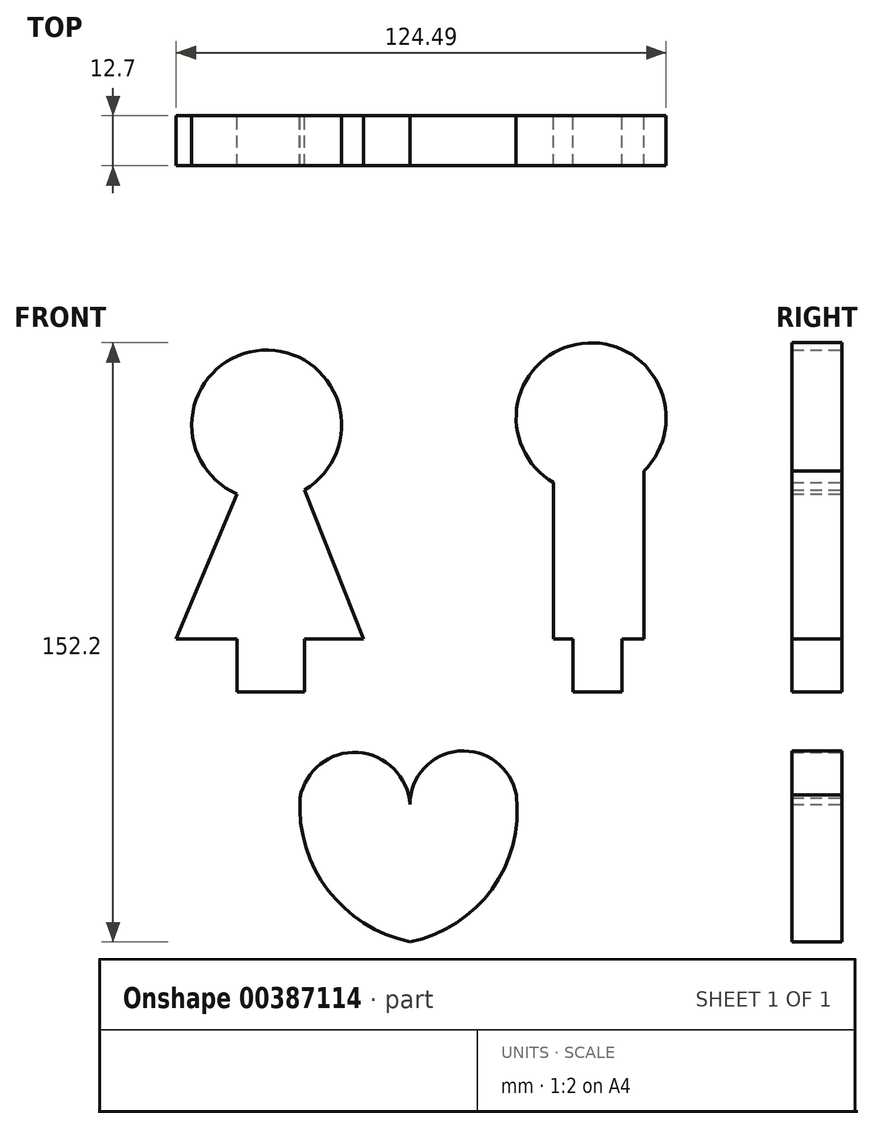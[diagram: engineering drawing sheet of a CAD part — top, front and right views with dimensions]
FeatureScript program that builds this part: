
annotation { "Feature Type Name" : "Feature", "Feature Type Description" : "" }
export const myFeature = defineFeature(function(context is Context, id is Id, definition is map)
    precondition{}
    {
        {
            var Q0;
            Q0=qCreatedBy(makeId("Front.planeOp"),FACE);
            var sketch = newSketch(context, id + "F0", { "sketchPlane" : qUnion([Q0])});
            skCircle(sketch, "E0", {"center": v(-36.38, 54.42) * mm, "radius": 19.05 * mm});
            skCircle(sketch, "E1", {"center": v(46.05, 56.26) * mm, "radius": 19.05 * mm});
            skLineSegment(sketch, "E2", {"start": v(-43.94, 36.93) * mm, "end": v(-59.39, 0) * mm});
            skLineSegment(sketch, "E3", {"start": v(-26.78, 37.97) * mm, "end": v(-11.72, 0) * mm});
            skLineSegment(sketch, "E4", {"start": v(36.5, 39.78) * mm, "end": v(36.5, 0) * mm});
            skLineSegment(sketch, "E5", {"start": v(59.4, 42.67) * mm, "end": v(59.4, 0) * mm});
            skLineSegment(sketch, "E6", {"start": v(-59.39, 0) * mm, "end": v(-11.72, 0) * mm});
            skLineSegment(sketch, "E7", {"start": v(36.5, 0) * mm, "end": v(59.4, 0) * mm});
            skLineSegment(sketch, "E8", {"start": v(-36.38, 0) * mm, "end": v(-36.38, -13.38) * mm});
            skLineSegment(sketch, "E9", {"start": v(-43.94, 0) * mm, "end": v(-43.94, -13.38) * mm});
            skLineSegment(sketch, "E10", {"start": v(-26.78, -13.38) * mm, "end": v(-43.94, -13.38) * mm});
            skLineSegment(sketch, "E11", {"start": v(-26.78, -13.38) * mm, "end": v(-26.78, 0) * mm});
            skLineSegment(sketch, "E12", {"start": v(41.44, -13.38) * mm, "end": v(41.44, 0) * mm});
            skLineSegment(sketch, "E13", {"start": v(53.9, 0) * mm, "end": v(53.9, -13.38) * mm});
            skLineSegment(sketch, "E14", {"start": v(41.44, -13.38) * mm, "end": v(53.9, -13.38) * mm});
            skLineSegment(sketch, "E15", {"start": v(47.68, -13.38) * mm, "end": v(47.68, 0) * mm});
            skPoint(sketch, "E16", {"position": v(0, -76.9) * mm});
            skArc(sketch, "E17", {"start": v(0, -42.01) * mm, "mid": v(-13.2, -28.8) * mm, "end": v(-27.92, -40.28) * mm});
            skArc(sketch, "E18", {"start": v(27.01, -39.54) * mm, "mid": v(12.38, -28.45) * mm, "end": v(0, -42.01) * mm});
            skArc(sketch, "E19", {"start": v(-27.92, -40.28) * mm, "mid": v(-20.77, -63.78) * mm, "end": v(0, -76.9) * mm});
            skArc(sketch, "E20", {"start": v(0, -76.9) * mm, "mid": v(20.82, -63.5) * mm, "end": v(27.01, -39.54) * mm});
            skSolve(sketch);
        }
        {
            var Q0;
            {var subQ0=sQuery(id+"F0.wireOp",EDGE,"E0");var subQ1=makeQuery(id+"F0.imprint","INTERSECT",VERTEX,{"derivedFrom":[subQ0,sQuery(id+"F0.wireOp",EDGE,"E2")]});Q0=makeQuery(id+"F0.imprint","IMPRINT",FACE,{"disambiguationData":[TD([[makeQuery(id+"F0.imprint","IMPRINT",EDGE,{"disambiguationData":[TD([[subQ1,-1.0]])],"derivedFrom":subQ0}),1.0]])]});}
            var Q1;
            {var subQ1=sQuery(id+"F0.wireOp",EDGE,"E2");Q1=makeQuery(id+"F0.imprint","IMPRINT",FACE,{"disambiguationData":[TD([[makeQuery(id+"F0.imprint","IMPRINT",EDGE,{"derivedFrom":subQ1}),1.0]])]});}
            var Q2;
            {var subQ0=sQuery(id+"F0.wireOp",EDGE,"E8");Q2=makeQuery(id+"F0.imprint","IMPRINT",FACE,{"disambiguationData":[TD([[makeQuery(id+"F0.imprint","IMPRINT",EDGE,{"derivedFrom":subQ0}),-1.0]])]});}
            var Q3;
            {var subQ0=sQuery(id+"F0.wireOp",EDGE,"E8");Q3=makeQuery(id+"F0.imprint","IMPRINT",FACE,{"disambiguationData":[TD([[makeQuery(id+"F0.imprint","IMPRINT",EDGE,{"derivedFrom":subQ0}),1.0]])]});}
            var Q4;
            Q4=makeQuery(id+"F0.imprint","IMPRINT",FACE,{"disambiguationData":[TD([[makeQuery(id+"F0.imprint","IMPRINT",EDGE,{"derivedFrom":sQuery(id+"F0.wireOp",EDGE,"E17")}),1.0]])]});
            var Q5;
            {var subQ0=sQuery(id+"F0.wireOp",EDGE,"E1");var subQ1=makeQuery(id+"F0.imprint","INTERSECT",VERTEX,{"derivedFrom":[subQ0,sQuery(id+"F0.wireOp",EDGE,"E4")]});Q5=makeQuery(id+"F0.imprint","IMPRINT",FACE,{"disambiguationData":[TD([[makeQuery(id+"F0.imprint","IMPRINT",EDGE,{"disambiguationData":[TD([[subQ1,-1.0]])],"derivedFrom":subQ0}),1.0]])]});}
            var Q6;
            {var subQ0=sQuery(id+"F0.wireOp",EDGE,"E4");Q6=makeQuery(id+"F0.imprint","IMPRINT",FACE,{"disambiguationData":[TD([[makeQuery(id+"F0.imprint","IMPRINT",EDGE,{"derivedFrom":subQ0}),1.0]])]});}
            var Q7;
            {var subQ0=sQuery(id+"F0.wireOp",EDGE,"E12");Q7=makeQuery(id+"F0.imprint","IMPRINT",FACE,{"disambiguationData":[TD([[makeQuery(id+"F0.imprint","IMPRINT",EDGE,{"derivedFrom":subQ0}),-1.0]])]});}
            var Q8;
            {var subQ0=sQuery(id+"F0.wireOp",EDGE,"E13");Q8=makeQuery(id+"F0.imprint","IMPRINT",FACE,{"disambiguationData":[TD([[makeQuery(id+"F0.imprint","IMPRINT",EDGE,{"derivedFrom":subQ0}),-1.0]])]});}
            extrude(context, id + "F1", {"entities" : qUnion([Q0, Q1, Q2, Q3, Q4, Q5, Q6, Q7, Q8]), "depth" : 12.7 * mm});
        }
    });
